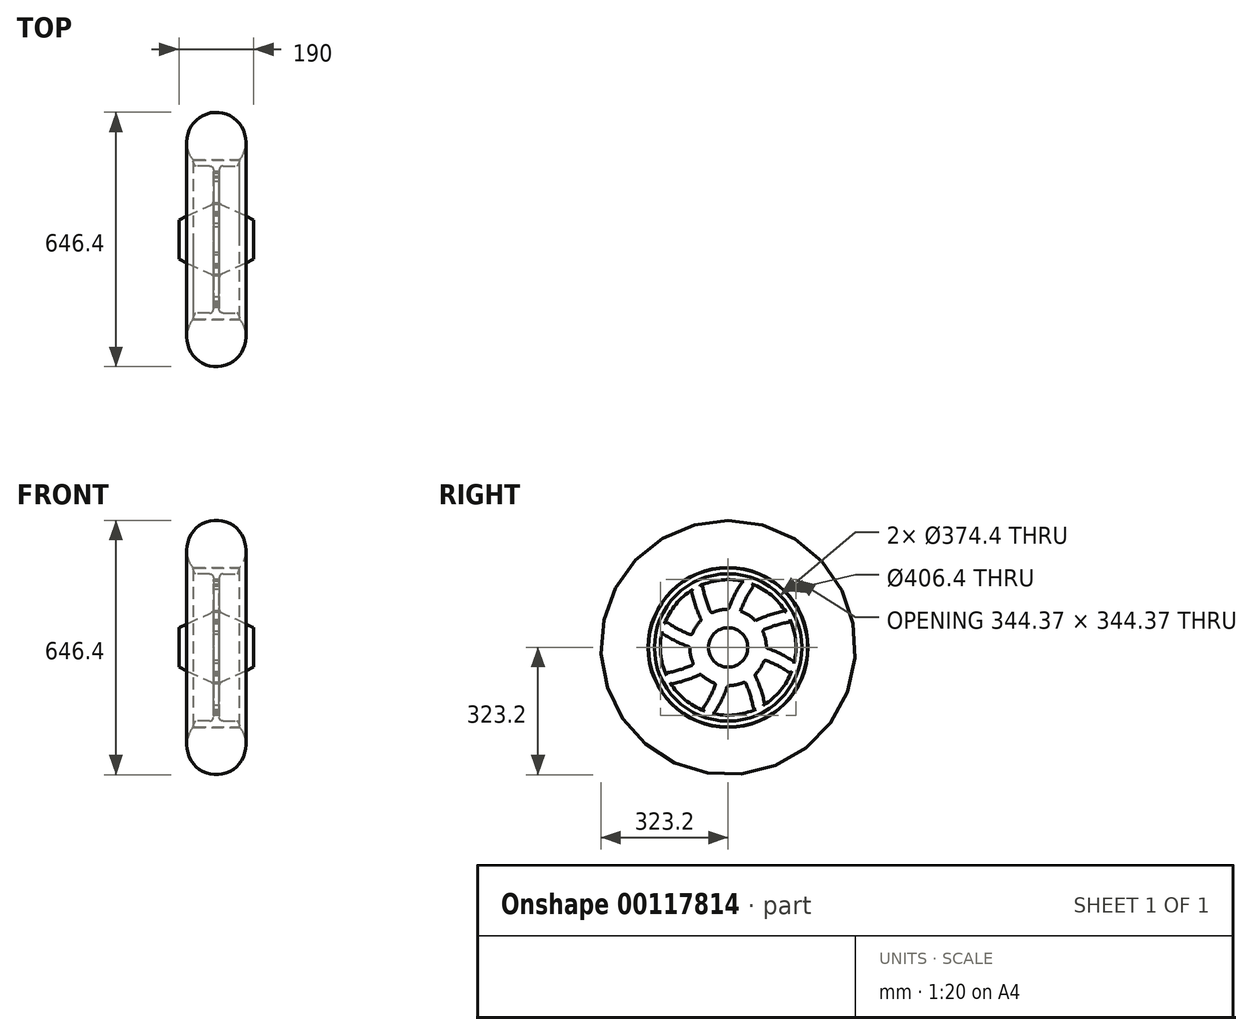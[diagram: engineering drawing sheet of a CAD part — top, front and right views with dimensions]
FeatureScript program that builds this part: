
annotation { "Feature Type Name" : "Feature", "Feature Type Description" : "" }
export const myFeature = defineFeature(function(context is Context, id is Id, definition is map)
    precondition{}
    {
        {
            var Q0;
            Q0=qCreatedBy(makeId("Front.planeOp"),FACE);
            var sketch = newSketch(context, id + "F0", { "sketchPlane" : qUnion([Q0])});
            skArc(sketch, "E0", {"start": v(0, 0) * mm, "mid": v(67.08, 41.46) * mm, "end": v(60, 120) * mm});
            skLineSegment(sketch, "E1", {"start": v(60, 120) * mm, "end": v(0, 120) * mm});
            skLineSegment(sketch, "E2", {"start": v(60, 121) * mm, "end": v(54.54, 136) * mm});
            skLineSegment(sketch, "E3", {"start": v(54.54, 136) * mm, "end": v(7.5, 136) * mm});
            skLineSegment(sketch, "E4", {"start": v(7.5, 136) * mm, "end": v(7.5, 232.4) * mm});
            skLineSegment(sketch, "E5", {"start": v(95, 323.2) * mm, "end": v(0, 323.2) * mm});
            skLineSegment(sketch, "E6", {"start": v(0, 323.2) * mm, "end": v(0, 121) * mm});
            skLineSegment(sketch, "E7", {"start": v(60, 120) * mm, "end": v(60, 121) * mm, "construction": true});
            skLineSegment(sketch, "E8", {"start": v(7.5, 232.4) * mm, "end": v(95, 273.2) * mm});
            skLineSegment(sketch, "E9", {"start": v(95, 273.2) * mm, "end": v(95, 323.2) * mm});
            skLineSegment(sketch, "E10", {"start": v(0, 121) * mm, "end": v(60, 121) * mm});
            skLineSegment(sketch, "E11", {"start": v(95, 273.2) * mm, "end": v(95, 0) * mm, "construction": true});
            skLineSegment(sketch, "E12.trimOffspring", {"start": v(0, 120) * mm, "end": v(0, 0) * mm});
            skSolve(sketch);
        }
        {
            var Q0;
            Q0=makeQuery(id+"F0.imprint","IMPRINT",FACE,{"disambiguationData":[TD([[makeQuery(id+"F0.imprint","IMPRINT",EDGE,{"derivedFrom":sQuery(id+"F0.wireOp",EDGE,"E0")}),1.0]])]});
            var Q1;
            Q1=makeQuery(id+"F0.imprint","IMPRINT",FACE,{"disambiguationData":[TD([[makeQuery(id+"F0.imprint","IMPRINT",EDGE,{"derivedFrom":sQuery(id+"F0.wireOp",EDGE,"E2")}),1.0]])]});
            var Q2;
            Q2=sQuery(id+"F0.wireOp",EDGE,"E5");
            revolve(context, id + "F1", {"entities" : qUnion([Q0, Q1]), "axis" : qUnion([Q2]), "revolveType" : RevolveType.FULL});
        }
        {
            var Q0;
            Q0=makeQuery(id+"F1.opRevolve","SWEPT_FACE",FACE,{"disambiguationData":[OSD([sQuery(id+"F0.wireOp",EDGE,"E4")])]});
            fillet(context, id + "F2", {"entities" : qUnion([Q0]), "radius" : 10 * mm, "tangentPropagation" : true, "allowEdgeOverflow" : false});
        }
        {
            var Q0;
            Q0=makeQuery(id+"F1.opRevolve","SWEPT_EDGE",EDGE,{"disambiguationData":[OSD([sQuery(id+"F0.wireOp",EDGE,"E2"),sQuery(id+"F0.wireOp",EDGE,"E3")])]});
            var Q1;
            Q1=makeQuery(id+"F1.opRevolve","SWEPT_EDGE",EDGE,{"disambiguationData":[OSD([sQuery(id+"F0.wireOp",EDGE,"E2"),sQuery(id+"F0.wireOp",EDGE,"E10")])]});
            var Q2;
            Q2=makeQuery(id+"F1.opRevolve","SWEPT_EDGE",EDGE,{"disambiguationData":[OSD([sQuery(id+"F0.wireOp",EDGE,"E0"),sQuery(id+"F0.wireOp",EDGE,"E1")])]});
            fillet(context, id + "F3", {"entities" : qUnion([Q0, Q1, Q2]), "radius" : 3 * mm, "tangentPropagation" : true, "allowEdgeOverflow" : false});
        }
        {
            var Q0;
            Q0=qCreatedBy(makeId("Right.planeOp"),FACE);
            var sketch = newSketch(context, id + "F4", { "sketchPlane" : qUnion([Q0])});
            skCircle(sketch, "E13.0.0", {"center": v(0, 323.2) * mm, "radius": 50 * mm, "construction": true});
            skCircle(sketch, "E14.0", {"center": v(0, 323.2) * mm, "radius": 177.2 * mm, "construction": true});
            skArc(sketch, "E15.0", {"start": v(66.63, 481.99) * mm, "mid": v(51.84, 487.41) * mm, "end": v(36.63, 491.46) * mm});
            skLineSegment(sketch, "E16", {"start": v(0, 323.2) * mm, "end": v(285, 323.2) * mm, "construction": true});
            skArc(sketch, "E17", {"start": v(1.17, 420.37) * mm, "mid": v(16.54, 457.1) * mm, "end": v(36.63, 491.46) * mm});
            skArc(sketch, "E18", {"start": v(31.17, 415.24) * mm, "mid": v(46.55, 449.86) * mm, "end": v(66.63, 481.99) * mm});
            skCircle(sketch, "E19", {"center": v(0, 323.2) * mm, "radius": 15 * mm, "construction": true});
            skArc(sketch, "E20.0", {"start": v(1.17, 420.37) * mm, "mid": v(16.37, 418.98) * mm, "end": v(31.17, 415.24) * mm});
            skSolve(sketch);
        }
        {
            var Q0;
            Q0=qCreatedBy(makeId("Right.planeOp"),FACE);
            var sketch = newSketch(context, id + "F5", { "sketchPlane" : qUnion([Q0])});
            skCircle(sketch, "E21.0", {"center": v(0, 323.2) * mm, "radius": 177.2 * mm, "construction": true});
            skCircle(sketch, "E21.1", {"center": v(0, 323.2) * mm, "radius": 97.17 * mm});
            skCircle(sketch, "E22.0", {"center": v(0, 323.2) * mm, "radius": 172.2 * mm});
            skSolve(sketch);
        }
        {
            var Q0;
            Q0=qSketchRegion(id+"F5",true);
            extrude(context, id + "F6", {"entities" : qUnion([Q0]), "operationType" : NewBodyOperationType.REMOVE, "endBound" : BoundingType.SYMMETRIC, "depth" : 50 * mm});
        }
        {
            var Q0;
            Q0=makeQuery(id+"F4.imprint","IMPRINT",FACE,{"disambiguationData":[TD([[makeQuery(id+"F4.imprint","IMPRINT",EDGE,{"derivedFrom":sQuery(id+"F4.wireOp",EDGE,"E15.0")}),1.0]])]});
            extrude(context, id + "F7", {"entities" : qUnion([Q0]), "depth" : 7.5 * mm});
        }
        {
            var Q0;
            Q0=makeQuery(id+"F7.opExtrude","SWEPT_BODY",BODY,{"disambiguationData":[OSD([sQuery(id+"F4.wireOp",EDGE,"E15.0"),sQuery(id+"F4.wireOp",EDGE,"E17"),sQuery(id+"F4.wireOp",EDGE,"E18"),sQuery(id+"F4.wireOp",EDGE,"E20.0")])]});
            var Q1;
            Q1=makeQuery(id+"F1.opRevolve","SWEPT_FACE",FACE,{"disambiguationData":[OSD([sQuery(id+"F0.wireOp",EDGE,"E8")])]});
            circularPattern(context, id + "F8", {"operationType" : NewBodyOperationType.ADD, "entities" : qUnion([Q0]), "axis" : qUnion([Q1]), "angle" : 45 * degree, "instanceCount" : 360 / 45});
        }
        {
            var Q0;
            Q0=makeQuery(id+"F8.opPattern","COPY",EDGE,{"derivedFrom":makeQuery(id+"F7.opExtrude","SWEPT_EDGE",EDGE,{"disambiguationData":[OSD([sQuery(id+"F4.wireOp",EDGE,"E15.0"),sQuery(id+"F4.wireOp",EDGE,"E17")])]}),"instanceName":"7"});
            var Q1;
            Q1=makeQuery(id+"F7.opExtrude","SWEPT_EDGE",EDGE,{"disambiguationData":[OSD([sQuery(id+"F4.wireOp",EDGE,"E15.0"),sQuery(id+"F4.wireOp",EDGE,"E17")])]});
            var Q2;
            Q2=makeQuery(id+"F8.opPattern","COPY",EDGE,{"derivedFrom":makeQuery(id+"F7.opExtrude","SWEPT_EDGE",EDGE,{"disambiguationData":[OSD([sQuery(id+"F4.wireOp",EDGE,"E15.0"),sQuery(id+"F4.wireOp",EDGE,"E18")])]}),"instanceName":"7"});
            var Q3;
            Q3=makeQuery(id+"F7.opExtrude","SWEPT_EDGE",EDGE,{"disambiguationData":[OSD([sQuery(id+"F4.wireOp",EDGE,"E15.0"),sQuery(id+"F4.wireOp",EDGE,"E18")])]});
            var Q4;
            Q4=makeQuery(id+"F8.opPattern","COPY",EDGE,{"derivedFrom":makeQuery(id+"F7.opExtrude","SWEPT_EDGE",EDGE,{"disambiguationData":[OSD([sQuery(id+"F4.wireOp",EDGE,"E15.0"),sQuery(id+"F4.wireOp",EDGE,"E17")])]}),"instanceName":"1"});
            var Q5;
            Q5=makeQuery(id+"F8.opPattern","COPY",EDGE,{"derivedFrom":makeQuery(id+"F7.opExtrude","SWEPT_EDGE",EDGE,{"disambiguationData":[OSD([sQuery(id+"F4.wireOp",EDGE,"E15.0"),sQuery(id+"F4.wireOp",EDGE,"E18")])]}),"instanceName":"1"});
            var Q6;
            Q6=makeQuery(id+"F8.opPattern","COPY",EDGE,{"derivedFrom":makeQuery(id+"F7.opExtrude","SWEPT_EDGE",EDGE,{"disambiguationData":[OSD([sQuery(id+"F4.wireOp",EDGE,"E15.0"),sQuery(id+"F4.wireOp",EDGE,"E17")])]}),"instanceName":"2"});
            var Q7;
            Q7=makeQuery(id+"F8.opPattern","COPY",EDGE,{"derivedFrom":makeQuery(id+"F7.opExtrude","SWEPT_EDGE",EDGE,{"disambiguationData":[OSD([sQuery(id+"F4.wireOp",EDGE,"E15.0"),sQuery(id+"F4.wireOp",EDGE,"E18")])]}),"instanceName":"2"});
            var Q8;
            Q8=makeQuery(id+"F8.opPattern","COPY",EDGE,{"derivedFrom":makeQuery(id+"F7.opExtrude","SWEPT_EDGE",EDGE,{"disambiguationData":[OSD([sQuery(id+"F4.wireOp",EDGE,"E15.0"),sQuery(id+"F4.wireOp",EDGE,"E17")])]}),"instanceName":"3"});
            var Q9;
            Q9=makeQuery(id+"F8.opPattern","COPY",EDGE,{"derivedFrom":makeQuery(id+"F7.opExtrude","SWEPT_EDGE",EDGE,{"disambiguationData":[OSD([sQuery(id+"F4.wireOp",EDGE,"E15.0"),sQuery(id+"F4.wireOp",EDGE,"E18")])]}),"instanceName":"4"});
            var Q10;
            Q10=makeQuery(id+"F8.opPattern","COPY",EDGE,{"derivedFrom":makeQuery(id+"F7.opExtrude","SWEPT_EDGE",EDGE,{"disambiguationData":[OSD([sQuery(id+"F4.wireOp",EDGE,"E15.0"),sQuery(id+"F4.wireOp",EDGE,"E18")])]}),"instanceName":"3"});
            var Q11;
            Q11=makeQuery(id+"F8.opPattern","COPY",EDGE,{"derivedFrom":makeQuery(id+"F7.opExtrude","SWEPT_EDGE",EDGE,{"disambiguationData":[OSD([sQuery(id+"F4.wireOp",EDGE,"E15.0"),sQuery(id+"F4.wireOp",EDGE,"E17")])]}),"instanceName":"4"});
            var Q12;
            Q12=makeQuery(id+"F8.opPattern","COPY",EDGE,{"derivedFrom":makeQuery(id+"F7.opExtrude","SWEPT_EDGE",EDGE,{"disambiguationData":[OSD([sQuery(id+"F4.wireOp",EDGE,"E15.0"),sQuery(id+"F4.wireOp",EDGE,"E18")])]}),"instanceName":"5"});
            var Q13;
            Q13=makeQuery(id+"F8.opPattern","COPY",EDGE,{"derivedFrom":makeQuery(id+"F7.opExtrude","SWEPT_EDGE",EDGE,{"disambiguationData":[OSD([sQuery(id+"F4.wireOp",EDGE,"E15.0"),sQuery(id+"F4.wireOp",EDGE,"E17")])]}),"instanceName":"5"});
            var Q14;
            Q14=makeQuery(id+"F8.opPattern","COPY",EDGE,{"derivedFrom":makeQuery(id+"F7.opExtrude","SWEPT_EDGE",EDGE,{"disambiguationData":[OSD([sQuery(id+"F4.wireOp",EDGE,"E15.0"),sQuery(id+"F4.wireOp",EDGE,"E18")])]}),"instanceName":"6"});
            var Q15;
            Q15=makeQuery(id+"F8.opPattern","COPY",EDGE,{"derivedFrom":makeQuery(id+"F7.opExtrude","SWEPT_EDGE",EDGE,{"disambiguationData":[OSD([sQuery(id+"F4.wireOp",EDGE,"E15.0"),sQuery(id+"F4.wireOp",EDGE,"E17")])]}),"instanceName":"6"});
            var Q16;
            Q16=makeQuery(id+"F8.opPattern","COPY",EDGE,{"derivedFrom":makeQuery(id+"F7.opExtrude","SWEPT_EDGE",EDGE,{"disambiguationData":[OSD([sQuery(id+"F4.wireOp",EDGE,"E17"),sQuery(id+"F4.wireOp",EDGE,"E20.0")])]}),"instanceName":"1"});
            var Q17;
            Q17=makeQuery(id+"F8.opPattern","COPY",EDGE,{"derivedFrom":makeQuery(id+"F7.opExtrude","SWEPT_EDGE",EDGE,{"disambiguationData":[OSD([sQuery(id+"F4.wireOp",EDGE,"E18"),sQuery(id+"F4.wireOp",EDGE,"E20.0")])]}),"instanceName":"7"});
            var Q18;
            Q18=makeQuery(id+"F7.opExtrude","SWEPT_EDGE",EDGE,{"disambiguationData":[OSD([sQuery(id+"F4.wireOp",EDGE,"E18"),sQuery(id+"F4.wireOp",EDGE,"E20.0")])]});
            var Q19;
            Q19=makeQuery(id+"F8.opPattern","COPY",EDGE,{"derivedFrom":makeQuery(id+"F7.opExtrude","SWEPT_EDGE",EDGE,{"disambiguationData":[OSD([sQuery(id+"F4.wireOp",EDGE,"E18"),sQuery(id+"F4.wireOp",EDGE,"E20.0")])]}),"instanceName":"1"});
            var Q20;
            Q20=makeQuery(id+"F8.opPattern","COPY",EDGE,{"derivedFrom":makeQuery(id+"F7.opExtrude","SWEPT_EDGE",EDGE,{"disambiguationData":[OSD([sQuery(id+"F4.wireOp",EDGE,"E17"),sQuery(id+"F4.wireOp",EDGE,"E20.0")])]}),"instanceName":"2"});
            var Q21;
            Q21=makeQuery(id+"F8.opPattern","COPY",EDGE,{"derivedFrom":makeQuery(id+"F7.opExtrude","SWEPT_EDGE",EDGE,{"disambiguationData":[OSD([sQuery(id+"F4.wireOp",EDGE,"E17"),sQuery(id+"F4.wireOp",EDGE,"E20.0")])]}),"instanceName":"3"});
            var Q22;
            Q22=makeQuery(id+"F8.opPattern","COPY",EDGE,{"derivedFrom":makeQuery(id+"F7.opExtrude","SWEPT_EDGE",EDGE,{"disambiguationData":[OSD([sQuery(id+"F4.wireOp",EDGE,"E18"),sQuery(id+"F4.wireOp",EDGE,"E20.0")])]}),"instanceName":"2"});
            var Q23;
            Q23=makeQuery(id+"F8.opPattern","COPY",EDGE,{"derivedFrom":makeQuery(id+"F7.opExtrude","SWEPT_EDGE",EDGE,{"disambiguationData":[OSD([sQuery(id+"F4.wireOp",EDGE,"E18"),sQuery(id+"F4.wireOp",EDGE,"E20.0")])]}),"instanceName":"3"});
            var Q24;
            Q24=makeQuery(id+"F8.opPattern","COPY",EDGE,{"derivedFrom":makeQuery(id+"F7.opExtrude","SWEPT_EDGE",EDGE,{"disambiguationData":[OSD([sQuery(id+"F4.wireOp",EDGE,"E17"),sQuery(id+"F4.wireOp",EDGE,"E20.0")])]}),"instanceName":"4"});
            var Q25;
            Q25=makeQuery(id+"F8.opPattern","COPY",EDGE,{"derivedFrom":makeQuery(id+"F7.opExtrude","SWEPT_EDGE",EDGE,{"disambiguationData":[OSD([sQuery(id+"F4.wireOp",EDGE,"E18"),sQuery(id+"F4.wireOp",EDGE,"E20.0")])]}),"instanceName":"4"});
            var Q26;
            Q26=makeQuery(id+"F8.opPattern","COPY",EDGE,{"derivedFrom":makeQuery(id+"F7.opExtrude","SWEPT_EDGE",EDGE,{"disambiguationData":[OSD([sQuery(id+"F4.wireOp",EDGE,"E17"),sQuery(id+"F4.wireOp",EDGE,"E20.0")])]}),"instanceName":"5"});
            var Q27;
            Q27=makeQuery(id+"F8.opPattern","COPY",EDGE,{"derivedFrom":makeQuery(id+"F7.opExtrude","SWEPT_EDGE",EDGE,{"disambiguationData":[OSD([sQuery(id+"F4.wireOp",EDGE,"E18"),sQuery(id+"F4.wireOp",EDGE,"E20.0")])]}),"instanceName":"5"});
            var Q28;
            Q28=makeQuery(id+"F8.opPattern","COPY",EDGE,{"derivedFrom":makeQuery(id+"F7.opExtrude","SWEPT_EDGE",EDGE,{"disambiguationData":[OSD([sQuery(id+"F4.wireOp",EDGE,"E17"),sQuery(id+"F4.wireOp",EDGE,"E20.0")])]}),"instanceName":"6"});
            var Q29;
            Q29=makeQuery(id+"F8.opPattern","COPY",EDGE,{"derivedFrom":makeQuery(id+"F7.opExtrude","SWEPT_EDGE",EDGE,{"disambiguationData":[OSD([sQuery(id+"F4.wireOp",EDGE,"E18"),sQuery(id+"F4.wireOp",EDGE,"E20.0")])]}),"instanceName":"6"});
            var Q30;
            Q30=makeQuery(id+"F8.opPattern","COPY",EDGE,{"derivedFrom":makeQuery(id+"F7.opExtrude","SWEPT_EDGE",EDGE,{"disambiguationData":[OSD([sQuery(id+"F4.wireOp",EDGE,"E17"),sQuery(id+"F4.wireOp",EDGE,"E20.0")])]}),"instanceName":"7"});
            var Q31;
            Q31=makeQuery(id+"F7.opExtrude","SWEPT_EDGE",EDGE,{"disambiguationData":[OSD([sQuery(id+"F4.wireOp",EDGE,"E17"),sQuery(id+"F4.wireOp",EDGE,"E20.0")])]});
            fillet(context, id + "F9", {"entities" : qUnion([Q0, Q1, Q2, Q3, Q4, Q5, Q6, Q7, Q8, Q9, Q10, Q11, Q12, Q13, Q14, Q15, Q16, Q17, Q18, Q19, Q20, Q21, Q22, Q23, Q24, Q25, Q26, Q27, Q28, Q29, Q30, Q31]), "radius" : 5 * mm, "tangentPropagation" : true, "allowEdgeOverflow" : false});
        }
        {
            var Q0;
            Q0=makeQuery(id+"F6.boolean.opBoolean","SPLIT",BODY,{"disambiguationData":[OD(0.0)],"derivedFrom":makeQuery(id+"F1.opRevolve","SWEPT_BODY",BODY,{"disambiguationData":[OSD([sQuery(id+"F0.wireOp",EDGE,"E0"),sQuery(id+"F0.wireOp",EDGE,"E1"),sQuery(id+"F0.wireOp",EDGE,"E2"),sQuery(id+"F0.wireOp",EDGE,"E3"),sQuery(id+"F0.wireOp",EDGE,"E4"),sQuery(id+"F0.wireOp",EDGE,"E5"),sQuery(id+"F0.wireOp",EDGE,"E6"),sQuery(id+"F0.wireOp",EDGE,"E8"),sQuery(id+"F0.wireOp",EDGE,"E9"),sQuery(id+"F0.wireOp",EDGE,"5frkVusw-xOTp-UwYc-Iyrz-2meRA9PvLd1T"),sQuery(id+"F0.wireOp",EDGE,"E10")])]})});
            var Q1;
            Q1=makeQuery(id+"F1.opRevolve","SWEPT_BODY",BODY,{"disambiguationData":[OSD([sQuery(id+"F0.wireOp",EDGE,"E0"),sQuery(id+"F0.wireOp",EDGE,"E1"),sQuery(id+"F0.wireOp",EDGE,"E12.trimOffspring")])]});
            var Q2;
            Q2=qCreatedBy(makeId("Right.planeOp"),FACE);
            mirror(context, id + "F10", {"operationType" : NewBodyOperationType.ADD, "entities" : qUnion([Q0, Q1]), "mirrorPlane" : qUnion([Q2])});
        }
    });
